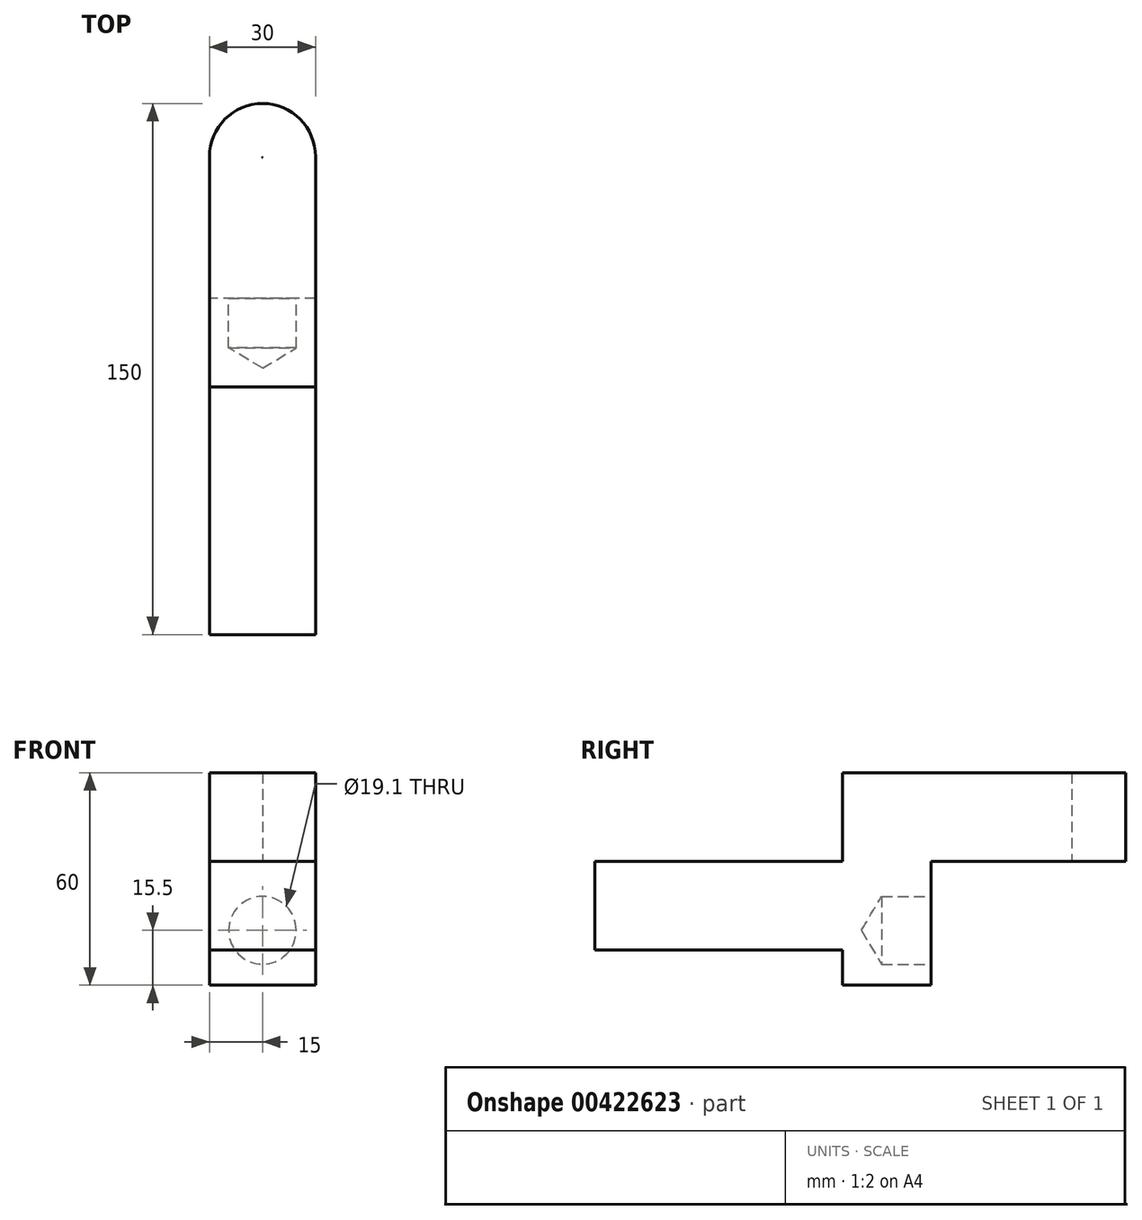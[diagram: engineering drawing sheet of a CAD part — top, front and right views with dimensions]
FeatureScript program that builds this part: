
annotation { "Feature Type Name" : "Feature", "Feature Type Description" : "" }
export const myFeature = defineFeature(function(context is Context, id is Id, definition is map)
    precondition{}
    {
        {
            var Q0;
            Q0=qCreatedBy(makeId("Right.planeOp"),FACE);
            var sketch = newSketch(context, id + "F0", { "sketchPlane" : qUnion([Q0])});
            skLineSegment(sketch, "E0", {"start": v(0, 0) * mm, "end": v(0, -35) * mm});
            skLineSegment(sketch, "E1", {"start": v(0, 0) * mm, "end": v(55, 0) * mm});
            skLineSegment(sketch, "E2", {"start": v(55, 0) * mm, "end": v(55, 25) * mm});
            skLineSegment(sketch, "E3", {"start": v(55, 25) * mm, "end": v(-25, 25) * mm});
            skLineSegment(sketch, "E4", {"start": v(-25, 25) * mm, "end": v(-25, 0) * mm});
            skLineSegment(sketch, "E5", {"start": v(-25, 0) * mm, "end": v(-95, 0) * mm});
            skLineSegment(sketch, "E6", {"start": v(-95, 0) * mm, "end": v(-95, -25) * mm});
            skLineSegment(sketch, "E7", {"start": v(-95, -25) * mm, "end": v(-25, -25) * mm});
            skLineSegment(sketch, "E8", {"start": v(-25, -25) * mm, "end": v(-25, -35) * mm});
            skLineSegment(sketch, "E9", {"start": v(-25, -35) * mm, "end": v(0, -35) * mm});
            skText(sketch, "E10", { "text": "Front <----", "fontName": "OpenSans-Regular.ttf"});
            const initialGuessF0  = {"E10": [-0.12384, 0.00333, 1, 0, 0.0075]};
            skSetInitialGuess(sketch, initialGuessF0);
            skSolve(sketch);
        }
        {
            var Q0;
            Q0=makeQuery(id+"F0.imprint","IMPRINT",FACE,{"disambiguationData":[TD([[makeQuery(id+"F0.imprint","IMPRINT",EDGE,{"derivedFrom":sQuery(id+"F0.wireOp",EDGE,"E0")}),-1.0]])]});
            extrude(context, id + "F1", {"entities" : qUnion([Q0]), "endBound" : BoundingType.SYMMETRIC, "depth" : 30 * mm});
        }
        {
            var Q0;
            Q0=makeQuery(id+"F1.opExtrude","SWEPT_FACE",FACE,{"disambiguationData":[OSD([sQuery(id+"F0.wireOp",EDGE,"E0")])]});
            var sketch = newSketch(context, id + "F2", { "sketchPlane" : qUnion([Q0])});
            skPoint(sketch, "E11", {"position": v(0, -19.5) * mm});
            skSolve(sketch);
        }
        {
            var Q0;
            Q0=sQuery(id+"F2.wireOp",VERTEX,"E11");
            var Q1;
            Q1=makeQuery(id+"F1.opExtrude","SWEPT_BODY",BODY,{"disambiguationData":[OSD([sQuery(id+"F0.wireOp",EDGE,"E0"),sQuery(id+"F0.wireOp",EDGE,"E1"),sQuery(id+"F0.wireOp",EDGE,"E2"),sQuery(id+"F0.wireOp",EDGE,"E3"),sQuery(id+"F0.wireOp",EDGE,"E4"),sQuery(id+"F0.wireOp",EDGE,"E5"),sQuery(id+"F0.wireOp",EDGE,"E6"),sQuery(id+"F0.wireOp",EDGE,"E7"),sQuery(id+"F0.wireOp",EDGE,"E8"),sQuery(id+"F0.wireOp",EDGE,"E9")])]});
            hole(context, id + "F3", {"style" : HoleStyle.SIMPLE, "endStyle" : HoleEndStyle.BLIND, "holeDiameter" : 19.1 * mm, "holeDepth" : 14 * mm, "isTappedThrough" : true, "tappedDepth" : 12 * mm, "tapClearance" : 3, "locations" : qUnion([Q0]), "scope" : qUnion([Q1])});
        }
        {
            var Q0;
            Q0=makeQuery(id+"F1.opExtrude","SWEPT_FACE",FACE,{"disambiguationData":[OSD([sQuery(id+"F0.wireOp",EDGE,"E1")])]});
            var sketch = newSketch(context, id + "F4", { "sketchPlane" : qUnion([Q0])});
            skPoint(sketch, "E12", {"position": v(0, -39.75) * mm});
            skSolve(sketch);
        }
        {
            var Q0;
            Q0=makeQuery(id+"F1.opExtrude","CAP_EDGE",EDGE,{"disambiguationData":[OSD([sQuery(id+"F0.wireOp",EDGE,"E2")])],"isStart":true});
            var Q1;
            Q1=makeQuery(id+"F1.opExtrude","CAP_EDGE",EDGE,{"disambiguationData":[OSD([sQuery(id+"F0.wireOp",EDGE,"E2")])],"isStart":false});
            fillet(context, id + "F5", {"entities" : qUnion([Q0, Q1]), "radius" : 15 * mm, "tangentPropagation" : true, "allowEdgeOverflow" : false});
        }
        {
            var Q0;
            Q0=sQuery(id+"F4.wireOp",VERTEX,"E12");
            var Q1;
            Q1=makeQuery(id+"F1.opExtrude","SWEPT_BODY",BODY,{"disambiguationData":[OSD([sQuery(id+"F0.wireOp",EDGE,"E0"),sQuery(id+"F0.wireOp",EDGE,"E1"),sQuery(id+"F0.wireOp",EDGE,"E2"),sQuery(id+"F0.wireOp",EDGE,"E3"),sQuery(id+"F0.wireOp",EDGE,"E4"),sQuery(id+"F0.wireOp",EDGE,"E5"),sQuery(id+"F0.wireOp",EDGE,"E6"),sQuery(id+"F0.wireOp",EDGE,"E7"),sQuery(id+"F0.wireOp",EDGE,"E8"),sQuery(id+"F0.wireOp",EDGE,"E9")])]});
            hole(context, id + "F6", {"style" : HoleStyle.SIMPLE, "endStyle" : HoleEndStyle.THROUGH, "standardTappedOrClearance" : lookupTablePath({ "standard" : "ANSI", "size" : "3/8 (0.38)", "type" : "Drilled" }), "standardBlindInLast" : lookupTablePath({ "standard" : "ANSI", "size" : "3/8", "type" : "Drilled" }), "holeDiameter" : 3 / 203.2 * mm, "isTappedThrough" : true, "tappedDepth" : 12 * mm, "tapClearance" : 3, "locations" : qUnion([Q0]), "scope" : qUnion([Q1])});
        }
    });
